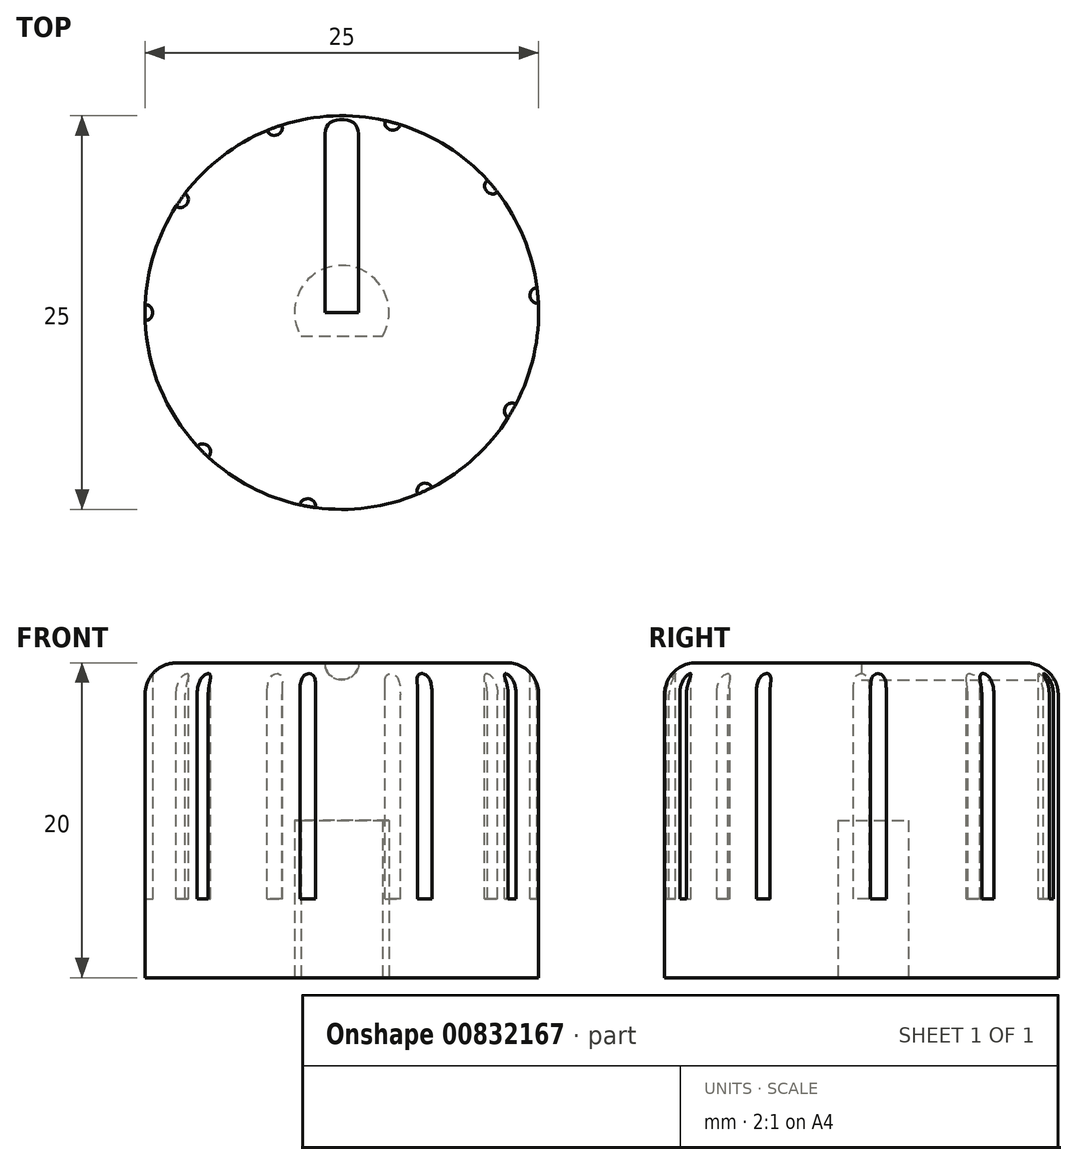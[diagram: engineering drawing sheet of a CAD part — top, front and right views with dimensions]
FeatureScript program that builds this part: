
annotation { "Feature Type Name" : "Feature", "Feature Type Description" : "" }
export const myFeature = defineFeature(function(context is Context, id is Id, definition is map)
    precondition{}
    {
        {
            var Q0;
            Q0=qCreatedBy(makeId("Top.planeOp"),FACE);
            var sketch = newSketch(context, id + "F0", { "sketchPlane" : qUnion([Q0])});
            skCircle(sketch, "E0", {"center": v(0, 0) * mm, "radius": 12.5 * mm});
            skCircle(sketch, "E1", {"center": v(0, 0) * mm, "radius": 3 * mm});
            skLineSegment(sketch, "E2", {"start": v(-2.6, -1.5) * mm, "end": v(2.6, -1.5) * mm});
            skSolve(sketch);
        }
        {
            var Q0;
            Q0=makeQuery(id+"F0.imprint","IMPRINT",FACE,{"disambiguationData":[TD([[makeQuery(id+"F0.imprint","IMPRINT",EDGE,{"derivedFrom":sQuery(id+"F0.wireOp",EDGE,"E0")}),1.0]])]});
            var Q1;
            {var subQ0=sQuery(id+"F0.wireOp",EDGE,"E2");Q1=makeQuery(id+"F0.imprint","IMPRINT",FACE,{"disambiguationData":[TD([[makeQuery(id+"F0.imprint","IMPRINT",EDGE,{"derivedFrom":subQ0}),-1.0]])]});}
            extrude(context, id + "F1", {"entities" : qUnion([Q0, Q1]), "depth" : 10 * mm, "offsetDistance" : 25 * mm});
        }
        {
            var Q0;
            Q0=makeQuery(id+"F1.opExtrude","CAP_FACE",FACE,{"disambiguationData":[OSD([sQuery(id+"F0.wireOp",EDGE,"E0"),sQuery(id+"F0.wireOp",EDGE,"E1"),sQuery(id+"F0.wireOp",EDGE,"E2")])],"isStart":false});
            var sketch = newSketch(context, id + "F2", { "sketchPlane" : qUnion([Q0])});
            skCircle(sketch, "E3", {"center": v(0, 0) * mm, "radius": 12.5 * mm});
            skSolve(sketch);
        }
        {
            var Q0;
            Q0=makeQuery(id+"F2.imprint","IMPRINT",FACE,{"disambiguationData":[TD([[makeQuery(id+"F2.imprint","IMPRINT",EDGE,{"derivedFrom":sQuery(id+"F2.wireOp",EDGE,"E3")}),1.0]])]});
            var Q1;
            Q1=makeQuery(id+"F2.imprint","IMPRINT",FACE,{"disambiguationData":[TD([[makeQuery(id+"F2.imprint","IMPRINT",EDGE,{"derivedFrom":makeQuery(id+"F1.opExtrude","CAP_EDGE",EDGE,{"disambiguationData":[OSD([sQuery(id+"F0.wireOp",EDGE,"E1")])],"isStart":false})}),1.0]])]});
            extrude(context, id + "F3", {"entities" : qUnion([Q0, Q1]), "operationType" : NewBodyOperationType.ADD, "depth" : 10 * mm, "offsetDistance" : 25 * mm});
        }
        {
            var Q0;
            Q0=makeQuery(id+"F3.opExtrude","CAP_FACE",FACE,{"disambiguationData":[OSD([sQuery(id+"F2.wireOp",EDGE,"E3")])],"isStart":false});
            var sketch = newSketch(context, id + "F4", { "sketchPlane" : qUnion([Q0])});
            skLineSegment(sketch, "E4", {"start": v(1.07, 0) * mm, "end": v(0, 0) * mm});
            skLineSegment(sketch, "E5", {"start": v(0, 0) * mm, "end": v(0, 12.81) * mm});
            skLineSegment(sketch, "E6", {"start": v(0, 12.81) * mm, "end": v(1.07, 12.81) * mm});
            skLineSegment(sketch, "E7", {"start": v(1.07, 12.81) * mm, "end": v(1.07, 0) * mm});
            skSolve(sketch);
        }
        {
            var Q0;
            {var subQ0=sQuery(id+"F4.wireOp",EDGE,"E4");Q0=makeQuery(id+"F4.imprint","IMPRINT",FACE,{"disambiguationData":[TD([[makeQuery(id+"F4.imprint","IMPRINT",EDGE,{"derivedFrom":subQ0}),-1.0]])]});}
            var Q1;
            {var subQ0=sQuery(id+"F4.wireOp",EDGE,"E6");Q1=makeQuery(id+"F4.imprint","IMPRINT",FACE,{"disambiguationData":[TD([[makeQuery(id+"F4.imprint","IMPRINT",EDGE,{"derivedFrom":subQ0}),-1.0]])]});}
            var Q2;
            Q2=sQuery(id+"F4.wireOp",EDGE,"E5");
            revolve(context, id + "F5", {"operationType" : NewBodyOperationType.REMOVE, "surfaceOperationType" : NewSurfaceOperationType.NEW, "entities" : qUnion([Q0, Q1]), "axis" : qUnion([Q2]), "revolveType" : RevolveType.FULL, "oppositeDirection" : true});
        }
        {
            var Q0;
            Q0=makeQuery(id+"F3.opExtrude","CAP_FACE",FACE,{"disambiguationData":[OSD([sQuery(id+"F2.wireOp",EDGE,"E3")])],"isStart":false});
            var sketch = newSketch(context, id + "F6", { "sketchPlane" : qUnion([Q0])});
            skLineSegment(sketch, "E8", {"start": v(0, 0) * mm, "end": v(-12.5, 0) * mm});
            skCircle(sketch, "E9", {"center": v(-12.5, 0) * mm, "radius": 0.5 * mm});
            skCircle(sketch, "E10.1.0", {"center": v(-10.24, 7.17) * mm, "radius": 0.5 * mm});
            skCircle(sketch, "E10.2.0", {"center": v(-4.28, 11.75) * mm, "radius": 0.5 * mm});
            skCircle(sketch, "E10.3.0", {"center": v(3.24, 12.07) * mm, "radius": 0.5 * mm});
            skCircle(sketch, "E10.4.0", {"center": v(9.58, 8.03) * mm, "radius": 0.5 * mm});
            skCircle(sketch, "E10.5.0", {"center": v(12.45, 1.09) * mm, "radius": 0.5 * mm});
            skCircle(sketch, "E10.6.0", {"center": v(10.83, -6.25) * mm, "radius": 0.5 * mm});
            skCircle(sketch, "E10.7.0", {"center": v(5.28, -11.33) * mm, "radius": 0.5 * mm});
            skCircle(sketch, "E10.8.0", {"center": v(-2.17, -12.31) * mm, "radius": 0.5 * mm});
            skCircle(sketch, "E10.9.0", {"center": v(-8.84, -8.84) * mm, "radius": 0.5 * mm});
            skPoint(sketch, "E10.center", {"position": v(0, 0) * mm});
            skLineSegment(sketch, "E10.anchor1", {"start": v(0, 0) * mm, "end": v(-12.5, 0) * mm, "construction": true});
            skLineSegment(sketch, "E10.anchor2", {"start": v(0, 0) * mm, "end": v(-8.84, -8.84) * mm, "construction": true});
            skSolve(sketch);
        }
        {
            var Q0;
            {var subQ0=sQuery(id+"F6.wireOp",EDGE,"E9");var subQ1=makeQuery(id+"F3.opExtrude","CAP_EDGE",EDGE,{"disambiguationData":[OSD([sQuery(id+"F2.wireOp",EDGE,"E3")])],"isStart":false});var subQ2=makeQuery(id+"F6.imprint","INTERSECT",VERTEX,{"disambiguationData":[OD(0.0)],"derivedFrom":[subQ1,subQ0]});Q0=makeQuery(id+"F6.imprint","IMPRINT",FACE,{"disambiguationData":[TD([[makeQuery(id+"F6.imprint","IMPRINT",EDGE,{"disambiguationData":[TD([[subQ2,-1.0]])],"derivedFrom":subQ0}),1.0]])]});}
            var Q1;
            {var subQ0=sQuery(id+"F6.wireOp",EDGE,"E8");var subQ1=makeQuery(id+"F3.opExtrude","CAP_EDGE",EDGE,{"disambiguationData":[OSD([sQuery(id+"F2.wireOp",EDGE,"E3")])],"isStart":false});var subQ2=makeQuery(id+"F6.imprint","INTERSECT",VERTEX,{"derivedFrom":[subQ1,subQ0]});Q1=makeQuery(id+"F6.imprint","IMPRINT",FACE,{"disambiguationData":[TD([[makeQuery(id+"F6.imprint","IMPRINT",EDGE,{"disambiguationData":[TD([[subQ2,1.0]])],"derivedFrom":subQ0}),1.0]])]});}
            var Q2;
            {var subQ0=sQuery(id+"F6.wireOp",EDGE,"E8");var subQ1=makeQuery(id+"F3.opExtrude","CAP_EDGE",EDGE,{"disambiguationData":[OSD([sQuery(id+"F2.wireOp",EDGE,"E3")])],"isStart":false});var subQ2=makeQuery(id+"F6.imprint","INTERSECT",VERTEX,{"derivedFrom":[subQ1,subQ0]});Q2=makeQuery(id+"F6.imprint","IMPRINT",FACE,{"disambiguationData":[TD([[makeQuery(id+"F6.imprint","IMPRINT",EDGE,{"disambiguationData":[TD([[subQ2,1.0]])],"derivedFrom":subQ0}),-1.0]])]});}
            var Q3;
            {var subQ0=sQuery(id+"F6.wireOp",EDGE,"E10.1.0");var subQ1=makeQuery(id+"F3.opExtrude","CAP_EDGE",EDGE,{"disambiguationData":[OSD([sQuery(id+"F2.wireOp",EDGE,"E3")])],"isStart":false});var subQ2=makeQuery(id+"F6.imprint","INTERSECT",VERTEX,{"disambiguationData":[OD(0.0)],"derivedFrom":[subQ1,subQ0]});Q3=makeQuery(id+"F6.imprint","IMPRINT",FACE,{"disambiguationData":[TD([[makeQuery(id+"F6.imprint","IMPRINT",EDGE,{"disambiguationData":[TD([[subQ2,-1.0]])],"derivedFrom":subQ0}),1.0]])]});}
            var Q4;
            {var subQ0=sQuery(id+"F6.wireOp",EDGE,"E10.1.0");var subQ1=makeQuery(id+"F3.opExtrude","CAP_EDGE",EDGE,{"disambiguationData":[OSD([sQuery(id+"F2.wireOp",EDGE,"E3")])],"isStart":false});var subQ2=makeQuery(id+"F6.imprint","INTERSECT",VERTEX,{"disambiguationData":[OD(0.0)],"derivedFrom":[subQ1,subQ0]});Q4=makeQuery(id+"F6.imprint","IMPRINT",FACE,{"disambiguationData":[TD([[makeQuery(id+"F6.imprint","IMPRINT",EDGE,{"disambiguationData":[TD([[subQ2,1.0]])],"derivedFrom":subQ0}),1.0]])]});}
            var Q5;
            {var subQ0=sQuery(id+"F6.wireOp",EDGE,"E10.2.0");var subQ1=makeQuery(id+"F3.opExtrude","CAP_EDGE",EDGE,{"disambiguationData":[OSD([sQuery(id+"F2.wireOp",EDGE,"E3")])],"isStart":false});var subQ2=makeQuery(id+"F6.imprint","INTERSECT",VERTEX,{"disambiguationData":[OD(0.0)],"derivedFrom":[subQ1,subQ0]});Q5=makeQuery(id+"F6.imprint","IMPRINT",FACE,{"disambiguationData":[TD([[makeQuery(id+"F6.imprint","IMPRINT",EDGE,{"disambiguationData":[TD([[subQ2,1.0]])],"derivedFrom":subQ0}),1.0]])]});}
            var Q6;
            {var subQ0=sQuery(id+"F6.wireOp",EDGE,"E10.2.0");var subQ1=makeQuery(id+"F3.opExtrude","CAP_EDGE",EDGE,{"disambiguationData":[OSD([sQuery(id+"F2.wireOp",EDGE,"E3")])],"isStart":false});var subQ2=makeQuery(id+"F6.imprint","INTERSECT",VERTEX,{"disambiguationData":[OD(0.0)],"derivedFrom":[subQ1,subQ0]});Q6=makeQuery(id+"F6.imprint","IMPRINT",FACE,{"disambiguationData":[TD([[makeQuery(id+"F6.imprint","IMPRINT",EDGE,{"disambiguationData":[TD([[subQ2,-1.0]])],"derivedFrom":subQ0}),1.0]])]});}
            var Q7;
            {var subQ0=sQuery(id+"F6.wireOp",EDGE,"E10.3.0");var subQ1=makeQuery(id+"F3.opExtrude","CAP_EDGE",EDGE,{"disambiguationData":[OSD([sQuery(id+"F2.wireOp",EDGE,"E3")])],"isStart":false});var subQ2=makeQuery(id+"F6.imprint","INTERSECT",VERTEX,{"disambiguationData":[OD(0.0)],"derivedFrom":[subQ1,subQ0]});Q7=makeQuery(id+"F6.imprint","IMPRINT",FACE,{"disambiguationData":[TD([[makeQuery(id+"F6.imprint","IMPRINT",EDGE,{"disambiguationData":[TD([[subQ2,1.0]])],"derivedFrom":subQ0}),1.0]])]});}
            var Q8;
            {var subQ0=sQuery(id+"F6.wireOp",EDGE,"E10.4.0");var subQ1=makeQuery(id+"F3.opExtrude","CAP_EDGE",EDGE,{"disambiguationData":[OSD([sQuery(id+"F2.wireOp",EDGE,"E3")])],"isStart":false});var subQ2=makeQuery(id+"F6.imprint","INTERSECT",VERTEX,{"disambiguationData":[OD(0.0)],"derivedFrom":[subQ1,subQ0]});Q8=makeQuery(id+"F6.imprint","IMPRINT",FACE,{"disambiguationData":[TD([[makeQuery(id+"F6.imprint","IMPRINT",EDGE,{"disambiguationData":[TD([[subQ2,1.0]])],"derivedFrom":subQ0}),1.0]])]});}
            var Q9;
            {var subQ0=sQuery(id+"F6.wireOp",EDGE,"E10.4.0");var subQ1=makeQuery(id+"F3.opExtrude","CAP_EDGE",EDGE,{"disambiguationData":[OSD([sQuery(id+"F2.wireOp",EDGE,"E3")])],"isStart":false});var subQ2=makeQuery(id+"F6.imprint","INTERSECT",VERTEX,{"disambiguationData":[OD(0.0)],"derivedFrom":[subQ1,subQ0]});Q9=makeQuery(id+"F6.imprint","IMPRINT",FACE,{"disambiguationData":[TD([[makeQuery(id+"F6.imprint","IMPRINT",EDGE,{"disambiguationData":[TD([[subQ2,-1.0]])],"derivedFrom":subQ0}),1.0]])]});}
            var Q10;
            {var subQ0=sQuery(id+"F6.wireOp",EDGE,"E10.5.0");var subQ1=makeQuery(id+"F3.opExtrude","CAP_EDGE",EDGE,{"disambiguationData":[OSD([sQuery(id+"F2.wireOp",EDGE,"E3")])],"isStart":false});var subQ2=makeQuery(id+"F6.imprint","INTERSECT",VERTEX,{"disambiguationData":[OD(0.0)],"derivedFrom":[subQ1,subQ0]});Q10=makeQuery(id+"F6.imprint","IMPRINT",FACE,{"disambiguationData":[TD([[makeQuery(id+"F6.imprint","IMPRINT",EDGE,{"disambiguationData":[TD([[subQ2,1.0]])],"derivedFrom":subQ0}),1.0]])]});}
            var Q11;
            {var subQ0=sQuery(id+"F6.wireOp",EDGE,"E10.5.0");var subQ1=makeQuery(id+"F3.opExtrude","CAP_EDGE",EDGE,{"disambiguationData":[OSD([sQuery(id+"F2.wireOp",EDGE,"E3")])],"isStart":false});var subQ2=makeQuery(id+"F6.imprint","INTERSECT",VERTEX,{"disambiguationData":[OD(0.0)],"derivedFrom":[subQ1,subQ0]});Q11=makeQuery(id+"F6.imprint","IMPRINT",FACE,{"disambiguationData":[TD([[makeQuery(id+"F6.imprint","IMPRINT",EDGE,{"disambiguationData":[TD([[subQ2,-1.0]])],"derivedFrom":subQ0}),1.0]])]});}
            var Q12;
            {var subQ0=sQuery(id+"F6.wireOp",EDGE,"E10.6.0");var subQ1=makeQuery(id+"F3.opExtrude","CAP_EDGE",EDGE,{"disambiguationData":[OSD([sQuery(id+"F2.wireOp",EDGE,"E3")])],"isStart":false});var subQ2=makeQuery(id+"F6.imprint","INTERSECT",VERTEX,{"disambiguationData":[OD(0.0)],"derivedFrom":[subQ1,subQ0]});Q12=makeQuery(id+"F6.imprint","IMPRINT",FACE,{"disambiguationData":[TD([[makeQuery(id+"F6.imprint","IMPRINT",EDGE,{"disambiguationData":[TD([[subQ2,1.0]])],"derivedFrom":subQ0}),1.0]])]});}
            var Q13;
            {var subQ0=sQuery(id+"F6.wireOp",EDGE,"E10.6.0");var subQ1=makeQuery(id+"F3.opExtrude","CAP_EDGE",EDGE,{"disambiguationData":[OSD([sQuery(id+"F2.wireOp",EDGE,"E3")])],"isStart":false});var subQ2=makeQuery(id+"F6.imprint","INTERSECT",VERTEX,{"disambiguationData":[OD(0.0)],"derivedFrom":[subQ1,subQ0]});Q13=makeQuery(id+"F6.imprint","IMPRINT",FACE,{"disambiguationData":[TD([[makeQuery(id+"F6.imprint","IMPRINT",EDGE,{"disambiguationData":[TD([[subQ2,-1.0]])],"derivedFrom":subQ0}),1.0]])]});}
            var Q14;
            {var subQ0=sQuery(id+"F6.wireOp",EDGE,"E10.7.0");var subQ1=makeQuery(id+"F3.opExtrude","CAP_EDGE",EDGE,{"disambiguationData":[OSD([sQuery(id+"F2.wireOp",EDGE,"E3")])],"isStart":false});var subQ2=makeQuery(id+"F6.imprint","INTERSECT",VERTEX,{"disambiguationData":[OD(0.0)],"derivedFrom":[subQ1,subQ0]});Q14=makeQuery(id+"F6.imprint","IMPRINT",FACE,{"disambiguationData":[TD([[makeQuery(id+"F6.imprint","IMPRINT",EDGE,{"disambiguationData":[TD([[subQ2,1.0]])],"derivedFrom":subQ0}),1.0]])]});}
            var Q15;
            {var subQ0=sQuery(id+"F6.wireOp",EDGE,"E10.7.0");var subQ1=makeQuery(id+"F3.opExtrude","CAP_EDGE",EDGE,{"disambiguationData":[OSD([sQuery(id+"F2.wireOp",EDGE,"E3")])],"isStart":false});var subQ2=makeQuery(id+"F6.imprint","INTERSECT",VERTEX,{"disambiguationData":[OD(0.0)],"derivedFrom":[subQ1,subQ0]});Q15=makeQuery(id+"F6.imprint","IMPRINT",FACE,{"disambiguationData":[TD([[makeQuery(id+"F6.imprint","IMPRINT",EDGE,{"disambiguationData":[TD([[subQ2,-1.0]])],"derivedFrom":subQ0}),1.0]])]});}
            var Q16;
            {var subQ0=sQuery(id+"F6.wireOp",EDGE,"E10.8.0");var subQ1=makeQuery(id+"F3.opExtrude","CAP_EDGE",EDGE,{"disambiguationData":[OSD([sQuery(id+"F2.wireOp",EDGE,"E3")])],"isStart":false});var subQ2=makeQuery(id+"F6.imprint","INTERSECT",VERTEX,{"disambiguationData":[OD(0.0)],"derivedFrom":[subQ1,subQ0]});Q16=makeQuery(id+"F6.imprint","IMPRINT",FACE,{"disambiguationData":[TD([[makeQuery(id+"F6.imprint","IMPRINT",EDGE,{"disambiguationData":[TD([[subQ2,1.0]])],"derivedFrom":subQ0}),1.0]])]});}
            var Q17;
            {var subQ0=sQuery(id+"F6.wireOp",EDGE,"E10.8.0");var subQ1=makeQuery(id+"F3.opExtrude","CAP_EDGE",EDGE,{"disambiguationData":[OSD([sQuery(id+"F2.wireOp",EDGE,"E3")])],"isStart":false});var subQ2=makeQuery(id+"F6.imprint","INTERSECT",VERTEX,{"disambiguationData":[OD(0.0)],"derivedFrom":[subQ1,subQ0]});Q17=makeQuery(id+"F6.imprint","IMPRINT",FACE,{"disambiguationData":[TD([[makeQuery(id+"F6.imprint","IMPRINT",EDGE,{"disambiguationData":[TD([[subQ2,-1.0]])],"derivedFrom":subQ0}),1.0]])]});}
            var Q18;
            {var subQ0=sQuery(id+"F6.wireOp",EDGE,"E10.9.0");var subQ1=makeQuery(id+"F3.opExtrude","CAP_EDGE",EDGE,{"disambiguationData":[OSD([sQuery(id+"F2.wireOp",EDGE,"E3")])],"isStart":false});var subQ2=makeQuery(id+"F6.imprint","INTERSECT",VERTEX,{"disambiguationData":[OD(0.0)],"derivedFrom":[subQ1,subQ0]});Q18=makeQuery(id+"F6.imprint","IMPRINT",FACE,{"disambiguationData":[TD([[makeQuery(id+"F6.imprint","IMPRINT",EDGE,{"disambiguationData":[TD([[subQ2,1.0]])],"derivedFrom":subQ0}),1.0]])]});}
            var Q19;
            {var subQ0=sQuery(id+"F6.wireOp",EDGE,"E10.9.0");var subQ1=makeQuery(id+"F3.opExtrude","CAP_EDGE",EDGE,{"disambiguationData":[OSD([sQuery(id+"F2.wireOp",EDGE,"E3")])],"isStart":false});var subQ2=makeQuery(id+"F6.imprint","INTERSECT",VERTEX,{"disambiguationData":[OD(0.0)],"derivedFrom":[subQ1,subQ0]});Q19=makeQuery(id+"F6.imprint","IMPRINT",FACE,{"disambiguationData":[TD([[makeQuery(id+"F6.imprint","IMPRINT",EDGE,{"disambiguationData":[TD([[subQ2,-1.0]])],"derivedFrom":subQ0}),1.0]])]});}
            var Q20;
            {var subQ0=sQuery(id+"F6.wireOp",EDGE,"E10.3.0");var subQ1=makeQuery(id+"F3.opExtrude","CAP_EDGE",EDGE,{"disambiguationData":[OSD([sQuery(id+"F2.wireOp",EDGE,"E3")])],"isStart":false});var subQ2=makeQuery(id+"F6.imprint","INTERSECT",VERTEX,{"disambiguationData":[OD(0.0)],"derivedFrom":[subQ1,subQ0]});Q20=makeQuery(id+"F6.imprint","IMPRINT",FACE,{"disambiguationData":[TD([[makeQuery(id+"F6.imprint","IMPRINT",EDGE,{"disambiguationData":[TD([[subQ2,-1.0]])],"derivedFrom":subQ0}),1.0]])]});}
            extrude(context, id + "F7", {"entities" : qUnion([Q0, Q1, Q2, Q3, Q4, Q5, Q6, Q7, Q8, Q9, Q10, Q11, Q12, Q13, Q14, Q15, Q16, Q17, Q18, Q19, Q20]), "operationType" : NewBodyOperationType.REMOVE, "oppositeDirection" : true, "depth" : 15 * mm, "offsetDistance" : 25 * mm});
        }
        {
            var Q0;
            {var subQ0=sQuery(id+"F2.wireOp",EDGE,"E3");Q0=makeQuery(id+"F7.boolean.opBoolean","SPLIT",EDGE,{"disambiguationData":[TD([makeQuery(id+"F1.opExtrude","SWEPT_FACE",FACE,{"disambiguationData":[OSD([sQuery(id+"F0.wireOp",EDGE,"E0")])]}),makeQuery(id+"F3.opExtrude","SWEPT_FACE",FACE,{"disambiguationData":[OSD([subQ0])]}),makeQuery(id+"F3.opExtrude","CAP_FACE",FACE,{"disambiguationData":[OSD([subQ0])],"isStart":false}),makeQuery(id+"F7.opExtrude","SWEPT_FACE",FACE,{"disambiguationData":[OSD([sQuery(id+"F6.wireOp",EDGE,"E10.1.0")])]}),makeQuery(id+"F7.opExtrude","SWEPT_FACE",FACE,{"disambiguationData":[OSD([sQuery(id+"F6.wireOp",EDGE,"E10.2.0")])]})])],"derivedFrom":makeQuery(id+"F3.opExtrude","CAP_EDGE",EDGE,{"disambiguationData":[OSD([subQ0])],"isStart":false})});}
            var Q1;
            {var subQ0=sQuery(id+"F2.wireOp",EDGE,"E3");Q1=makeQuery(id+"F7.boolean.opBoolean","SPLIT",EDGE,{"disambiguationData":[TD([makeQuery(id+"F1.opExtrude","SWEPT_FACE",FACE,{"disambiguationData":[OSD([sQuery(id+"F0.wireOp",EDGE,"E0")])]}),makeQuery(id+"F3.opExtrude","SWEPT_FACE",FACE,{"disambiguationData":[OSD([subQ0])]}),makeQuery(id+"F3.opExtrude","CAP_FACE",FACE,{"disambiguationData":[OSD([subQ0])],"isStart":false}),makeQuery(id+"F5.boolean.opBoolean","COPY",FACE,{"derivedFrom":makeQuery(id+"F5.opRevolve","SWEPT_FACE",FACE,{"disambiguationData":[OSD([sQuery(id+"F4.wireOp",EDGE,"E7")])]})}),makeQuery(id+"F7.opExtrude","SWEPT_FACE",FACE,{"disambiguationData":[OSD([sQuery(id+"F6.wireOp",EDGE,"E10.2.0")])]})])],"derivedFrom":makeQuery(id+"F3.opExtrude","CAP_EDGE",EDGE,{"disambiguationData":[OSD([subQ0])],"isStart":false})});}
            var Q2;
            {var subQ0=sQuery(id+"F2.wireOp",EDGE,"E3");Q2=makeQuery(id+"F7.boolean.opBoolean","SPLIT",EDGE,{"disambiguationData":[TD([makeQuery(id+"F1.opExtrude","SWEPT_FACE",FACE,{"disambiguationData":[OSD([sQuery(id+"F0.wireOp",EDGE,"E0")])]}),makeQuery(id+"F3.opExtrude","SWEPT_FACE",FACE,{"disambiguationData":[OSD([subQ0])]}),makeQuery(id+"F3.opExtrude","CAP_FACE",FACE,{"disambiguationData":[OSD([subQ0])],"isStart":false}),makeQuery(id+"F5.boolean.opBoolean","COPY",FACE,{"derivedFrom":makeQuery(id+"F5.opRevolve","SWEPT_FACE",FACE,{"disambiguationData":[OSD([sQuery(id+"F4.wireOp",EDGE,"E7")])]})}),makeQuery(id+"F7.opExtrude","SWEPT_FACE",FACE,{"disambiguationData":[OSD([sQuery(id+"F6.wireOp",EDGE,"E10.3.0")])]})])],"derivedFrom":makeQuery(id+"F3.opExtrude","CAP_EDGE",EDGE,{"disambiguationData":[OSD([subQ0])],"isStart":false})});}
            var Q3;
            {var subQ0=sQuery(id+"F2.wireOp",EDGE,"E3");Q3=makeQuery(id+"F7.boolean.opBoolean","SPLIT",EDGE,{"disambiguationData":[TD([makeQuery(id+"F1.opExtrude","SWEPT_FACE",FACE,{"disambiguationData":[OSD([sQuery(id+"F0.wireOp",EDGE,"E0")])]}),makeQuery(id+"F3.opExtrude","SWEPT_FACE",FACE,{"disambiguationData":[OSD([subQ0])]}),makeQuery(id+"F3.opExtrude","CAP_FACE",FACE,{"disambiguationData":[OSD([subQ0])],"isStart":false}),makeQuery(id+"F7.opExtrude","SWEPT_FACE",FACE,{"disambiguationData":[OSD([sQuery(id+"F6.wireOp",EDGE,"E10.3.0")])]}),makeQuery(id+"F7.opExtrude","SWEPT_FACE",FACE,{"disambiguationData":[OSD([sQuery(id+"F6.wireOp",EDGE,"E10.4.0")])]})])],"derivedFrom":makeQuery(id+"F3.opExtrude","CAP_EDGE",EDGE,{"disambiguationData":[OSD([subQ0])],"isStart":false})});}
            var Q4;
            {var subQ0=sQuery(id+"F2.wireOp",EDGE,"E3");Q4=makeQuery(id+"F7.boolean.opBoolean","SPLIT",EDGE,{"disambiguationData":[TD([makeQuery(id+"F1.opExtrude","SWEPT_FACE",FACE,{"disambiguationData":[OSD([sQuery(id+"F0.wireOp",EDGE,"E0")])]}),makeQuery(id+"F3.opExtrude","SWEPT_FACE",FACE,{"disambiguationData":[OSD([subQ0])]}),makeQuery(id+"F3.opExtrude","CAP_FACE",FACE,{"disambiguationData":[OSD([subQ0])],"isStart":false}),makeQuery(id+"F7.opExtrude","SWEPT_FACE",FACE,{"disambiguationData":[OSD([sQuery(id+"F6.wireOp",EDGE,"E10.4.0")])]}),makeQuery(id+"F7.opExtrude","SWEPT_FACE",FACE,{"disambiguationData":[OSD([sQuery(id+"F6.wireOp",EDGE,"E10.5.0")])]})])],"derivedFrom":makeQuery(id+"F3.opExtrude","CAP_EDGE",EDGE,{"disambiguationData":[OSD([subQ0])],"isStart":false})});}
            var Q5;
            {var subQ0=sQuery(id+"F2.wireOp",EDGE,"E3");Q5=makeQuery(id+"F7.boolean.opBoolean","SPLIT",EDGE,{"disambiguationData":[TD([makeQuery(id+"F1.opExtrude","SWEPT_FACE",FACE,{"disambiguationData":[OSD([sQuery(id+"F0.wireOp",EDGE,"E0")])]}),makeQuery(id+"F3.opExtrude","SWEPT_FACE",FACE,{"disambiguationData":[OSD([subQ0])]}),makeQuery(id+"F3.opExtrude","CAP_FACE",FACE,{"disambiguationData":[OSD([subQ0])],"isStart":false}),makeQuery(id+"F7.opExtrude","SWEPT_FACE",FACE,{"disambiguationData":[OSD([sQuery(id+"F6.wireOp",EDGE,"E9")])]}),makeQuery(id+"F7.opExtrude","SWEPT_FACE",FACE,{"disambiguationData":[OSD([sQuery(id+"F6.wireOp",EDGE,"E10.1.0")])]})])],"derivedFrom":makeQuery(id+"F3.opExtrude","CAP_EDGE",EDGE,{"disambiguationData":[OSD([subQ0])],"isStart":false})});}
            var Q6;
            {var subQ0=sQuery(id+"F2.wireOp",EDGE,"E3");Q6=makeQuery(id+"F7.boolean.opBoolean","SPLIT",EDGE,{"disambiguationData":[TD([makeQuery(id+"F1.opExtrude","SWEPT_FACE",FACE,{"disambiguationData":[OSD([sQuery(id+"F0.wireOp",EDGE,"E0")])]}),makeQuery(id+"F3.opExtrude","SWEPT_FACE",FACE,{"disambiguationData":[OSD([subQ0])]}),makeQuery(id+"F3.opExtrude","CAP_FACE",FACE,{"disambiguationData":[OSD([subQ0])],"isStart":false}),makeQuery(id+"F7.opExtrude","SWEPT_FACE",FACE,{"disambiguationData":[OSD([sQuery(id+"F6.wireOp",EDGE,"E9")])]}),makeQuery(id+"F7.opExtrude","SWEPT_FACE",FACE,{"disambiguationData":[OSD([sQuery(id+"F6.wireOp",EDGE,"E10.9.0")])]})])],"derivedFrom":makeQuery(id+"F3.opExtrude","CAP_EDGE",EDGE,{"disambiguationData":[OSD([subQ0])],"isStart":false})});}
            var Q7;
            {var subQ0=sQuery(id+"F2.wireOp",EDGE,"E3");Q7=makeQuery(id+"F7.boolean.opBoolean","SPLIT",EDGE,{"disambiguationData":[TD([makeQuery(id+"F1.opExtrude","SWEPT_FACE",FACE,{"disambiguationData":[OSD([sQuery(id+"F0.wireOp",EDGE,"E0")])]}),makeQuery(id+"F3.opExtrude","SWEPT_FACE",FACE,{"disambiguationData":[OSD([subQ0])]}),makeQuery(id+"F3.opExtrude","CAP_FACE",FACE,{"disambiguationData":[OSD([subQ0])],"isStart":false}),makeQuery(id+"F7.opExtrude","SWEPT_FACE",FACE,{"disambiguationData":[OSD([sQuery(id+"F6.wireOp",EDGE,"E10.8.0")])]}),makeQuery(id+"F7.opExtrude","SWEPT_FACE",FACE,{"disambiguationData":[OSD([sQuery(id+"F6.wireOp",EDGE,"E10.9.0")])]})])],"derivedFrom":makeQuery(id+"F3.opExtrude","CAP_EDGE",EDGE,{"disambiguationData":[OSD([subQ0])],"isStart":false})});}
            var Q8;
            {var subQ0=sQuery(id+"F2.wireOp",EDGE,"E3");Q8=makeQuery(id+"F7.boolean.opBoolean","SPLIT",EDGE,{"disambiguationData":[TD([makeQuery(id+"F1.opExtrude","SWEPT_FACE",FACE,{"disambiguationData":[OSD([sQuery(id+"F0.wireOp",EDGE,"E0")])]}),makeQuery(id+"F3.opExtrude","SWEPT_FACE",FACE,{"disambiguationData":[OSD([subQ0])]}),makeQuery(id+"F3.opExtrude","CAP_FACE",FACE,{"disambiguationData":[OSD([subQ0])],"isStart":false}),makeQuery(id+"F7.opExtrude","SWEPT_FACE",FACE,{"disambiguationData":[OSD([sQuery(id+"F6.wireOp",EDGE,"E10.7.0")])]}),makeQuery(id+"F7.opExtrude","SWEPT_FACE",FACE,{"disambiguationData":[OSD([sQuery(id+"F6.wireOp",EDGE,"E10.8.0")])]})])],"derivedFrom":makeQuery(id+"F3.opExtrude","CAP_EDGE",EDGE,{"disambiguationData":[OSD([subQ0])],"isStart":false})});}
            var Q9;
            {var subQ0=sQuery(id+"F2.wireOp",EDGE,"E3");Q9=makeQuery(id+"F7.boolean.opBoolean","SPLIT",EDGE,{"disambiguationData":[TD([makeQuery(id+"F1.opExtrude","SWEPT_FACE",FACE,{"disambiguationData":[OSD([sQuery(id+"F0.wireOp",EDGE,"E0")])]}),makeQuery(id+"F3.opExtrude","SWEPT_FACE",FACE,{"disambiguationData":[OSD([subQ0])]}),makeQuery(id+"F3.opExtrude","CAP_FACE",FACE,{"disambiguationData":[OSD([subQ0])],"isStart":false}),makeQuery(id+"F7.opExtrude","SWEPT_FACE",FACE,{"disambiguationData":[OSD([sQuery(id+"F6.wireOp",EDGE,"E10.6.0")])]}),makeQuery(id+"F7.opExtrude","SWEPT_FACE",FACE,{"disambiguationData":[OSD([sQuery(id+"F6.wireOp",EDGE,"E10.7.0")])]})])],"derivedFrom":makeQuery(id+"F3.opExtrude","CAP_EDGE",EDGE,{"disambiguationData":[OSD([subQ0])],"isStart":false})});}
            var Q10;
            {var subQ0=sQuery(id+"F2.wireOp",EDGE,"E3");Q10=makeQuery(id+"F7.boolean.opBoolean","SPLIT",EDGE,{"disambiguationData":[TD([makeQuery(id+"F1.opExtrude","SWEPT_FACE",FACE,{"disambiguationData":[OSD([sQuery(id+"F0.wireOp",EDGE,"E0")])]}),makeQuery(id+"F3.opExtrude","SWEPT_FACE",FACE,{"disambiguationData":[OSD([subQ0])]}),makeQuery(id+"F3.opExtrude","CAP_FACE",FACE,{"disambiguationData":[OSD([subQ0])],"isStart":false}),makeQuery(id+"F7.opExtrude","SWEPT_FACE",FACE,{"disambiguationData":[OSD([sQuery(id+"F6.wireOp",EDGE,"E10.5.0")])]}),makeQuery(id+"F7.opExtrude","SWEPT_FACE",FACE,{"disambiguationData":[OSD([sQuery(id+"F6.wireOp",EDGE,"E10.6.0")])]})])],"derivedFrom":makeQuery(id+"F3.opExtrude","CAP_EDGE",EDGE,{"disambiguationData":[OSD([subQ0])],"isStart":false})});}
            fillet(context, id + "F8", {"entities" : qUnion([Q0, Q1, Q2, Q3, Q4, Q5, Q6, Q7, Q8, Q9, Q10]), "radius" : 2 * mm, "tangentPropagation" : true, "allowEdgeOverflow" : false});
        }
        {
            var Q0;
            {var subQ0=sQuery(id+"F6.wireOp",EDGE,"E10.9.0");var subQ1=makeQuery(id+"F3.opExtrude","CAP_EDGE",EDGE,{"disambiguationData":[OSD([sQuery(id+"F2.wireOp",EDGE,"E3")])],"isStart":false});var subQ2=makeQuery(id+"F6.imprint","INTERSECT",VERTEX,{"disambiguationData":[OD(0.0)],"derivedFrom":[subQ1,subQ0]});Q0=makeQuery(id+"F6.imprint","IMPRINT",FACE,{"disambiguationData":[TD([[makeQuery(id+"F6.imprint","IMPRINT",EDGE,{"disambiguationData":[TD([[subQ2,-1.0]])],"derivedFrom":subQ0}),1.0]])]});}
            var Q1;
            {var subQ0=sQuery(id+"F6.wireOp",EDGE,"E10.9.0");var subQ1=makeQuery(id+"F3.opExtrude","CAP_EDGE",EDGE,{"disambiguationData":[OSD([sQuery(id+"F2.wireOp",EDGE,"E3")])],"isStart":false});var subQ2=makeQuery(id+"F6.imprint","INTERSECT",VERTEX,{"disambiguationData":[OD(0.0)],"derivedFrom":[subQ1,subQ0]});Q1=makeQuery(id+"F6.imprint","IMPRINT",FACE,{"disambiguationData":[TD([[makeQuery(id+"F6.imprint","IMPRINT",EDGE,{"disambiguationData":[TD([[subQ2,1.0]])],"derivedFrom":subQ0}),1.0]])]});}
            var Q2;
            {var subQ0=sQuery(id+"F6.wireOp",EDGE,"E10.8.0");var subQ1=makeQuery(id+"F3.opExtrude","CAP_EDGE",EDGE,{"disambiguationData":[OSD([sQuery(id+"F2.wireOp",EDGE,"E3")])],"isStart":false});var subQ2=makeQuery(id+"F6.imprint","INTERSECT",VERTEX,{"disambiguationData":[OD(0.0)],"derivedFrom":[subQ1,subQ0]});Q2=makeQuery(id+"F6.imprint","IMPRINT",FACE,{"disambiguationData":[TD([[makeQuery(id+"F6.imprint","IMPRINT",EDGE,{"disambiguationData":[TD([[subQ2,-1.0]])],"derivedFrom":subQ0}),1.0]])]});}
            var Q3;
            Q3=sQuery(id+"F6.wireOp",EDGE,"E9");
            var Q4;
            Q4=sQuery(id+"F6.wireOp",EDGE,"E10.1.0");
            var Q5;
            Q5=sQuery(id+"F6.wireOp",EDGE,"E10.2.0");
            var Q6;
            Q6=sQuery(id+"F6.wireOp",EDGE,"E10.3.0");
            var Q7;
            Q7=sQuery(id+"F6.wireOp",EDGE,"E10.4.0");
            var Q8;
            Q8=sQuery(id+"F6.wireOp",EDGE,"E10.5.0");
            var Q9;
            Q9=sQuery(id+"F6.wireOp",EDGE,"E10.6.0");
            var Q10;
            Q10=sQuery(id+"F6.wireOp",EDGE,"E10.7.0");
            var Q11;
            Q11=sQuery(id+"F6.wireOp",EDGE,"E10.8.0");
            var Q12;
            Q12=sQuery(id+"F6.wireOp",EDGE,"E10.9.0");
            extrude(context, id + "F9", {"entities" : qUnion([Q0, Q1, Q2]), "operationType" : NewBodyOperationType.REMOVE, "surfaceEntities" : qUnion([Q3, Q4, Q5, Q6, Q7, Q8, Q9, Q10, Q11, Q12]), "oppositeDirection" : true, "depth" : 15 * mm, "offsetDistance" : 25 * mm});
        }
    });
